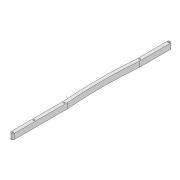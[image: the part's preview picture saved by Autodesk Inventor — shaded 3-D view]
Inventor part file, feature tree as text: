
AUTODESK INVENTOR PART (.ipt)
format: ipt  version: 2022 (Build 260153000, 153)  size: 107,520 bytes
history: native  units: mm
features: extrude x1, sketch x1
ambient origin geometry x8: Origin, YZ Plane, XZ Plane, XY Plane, X Axis, Y Axis, Z Axis, Center Point
bodies: Solid1 (feature_tree)
feature tree (2):
  extrude  "Extrusion1"  Depth=287.501mm
  sketch  "Sketch1"  dims[d0=6.0mm d1=287.501mm d2=3.0mm d3=3.0mm d4=10.0mm d5=0.0mm d14=3.0mm d15=39.171mm d16=3.0mm d17=94.738mm d18=3.0mm d19=233.822mm d20=800.0mm d21=800.0mm d22=3.0mm d23=3.0mm]
